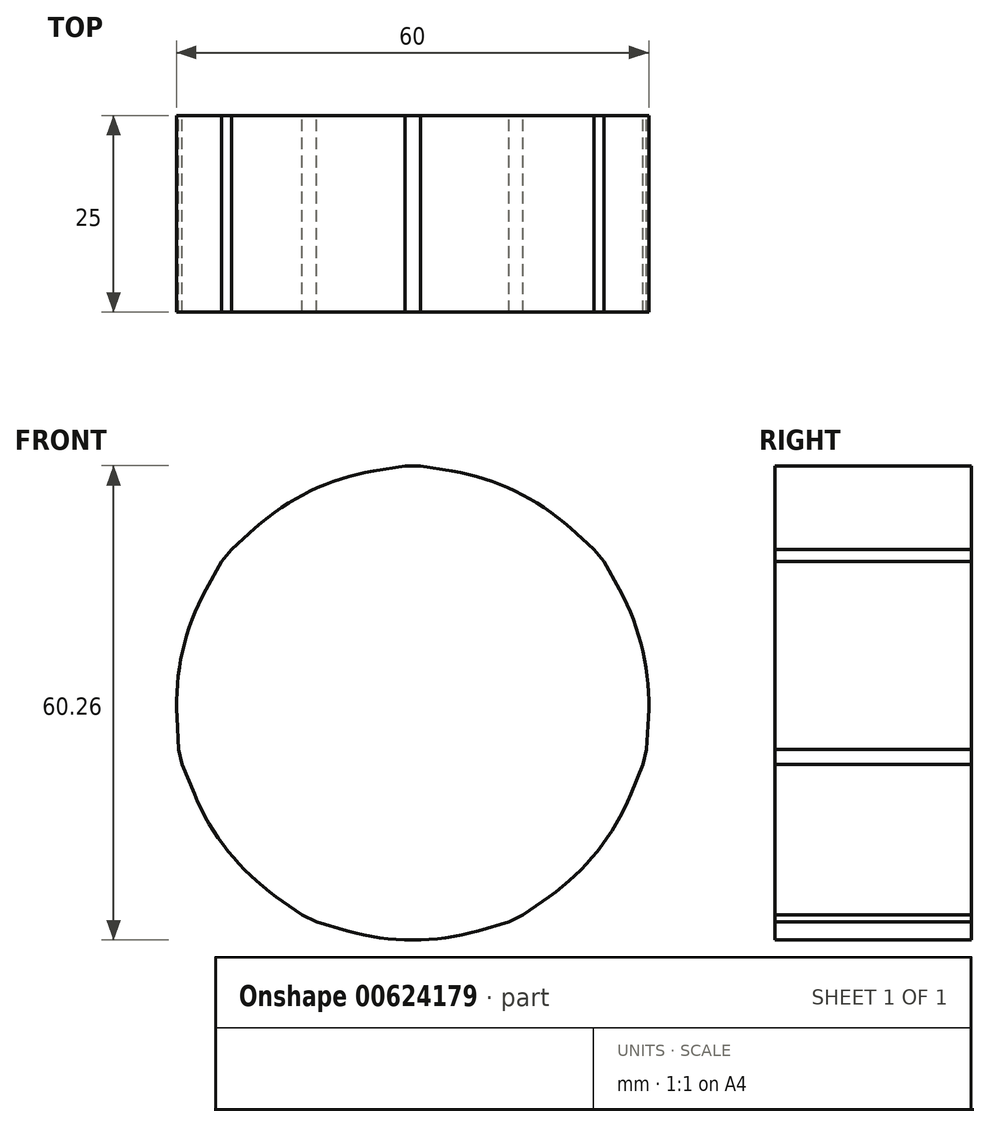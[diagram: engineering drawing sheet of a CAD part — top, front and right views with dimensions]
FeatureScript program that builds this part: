
annotation { "Feature Type Name" : "Feature", "Feature Type Description" : "" }
export const myFeature = defineFeature(function(context is Context, id is Id, definition is map)
    precondition{}
    {
        {
            assignVariable(context, id + "F0", {"name" : "pinon", "anyValue" : 14});
        }
        {
            assignVariable(context, id + "F1", {"name" : "a", "anyValue" : 2});
        }
        {
            assignVariable(context, id + "F2", {"name" : "b", "anyValue" : getVariable(context, 'pinon') / getVariable(context, 'a')});
        }
        {
            var Q0;
            Q0=qCreatedBy(makeId("Front.planeOp"),FACE);
            var sketch = newSketch(context, id + "F3", { "sketchPlane" : qUnion([Q0])});
            skCircle(sketch, "E0", {"center": v(0, 0) * mm, "radius": 30 * mm});
            skLineSegment(sketch, "E1", {"start": v(0, 30.26) * mm, "end": v(1, 30.26) * mm});
            skLineSegment(sketch, "E2", {"start": v(1, 30.26) * mm, "end": v(5, 29.58) * mm});
            skLineSegment(sketch, "E3", {"start": v(0, 55.33) * mm, "end": v(0, 84) * mm, "construction": true});
            skLineSegment(sketch, "E4.MirrorCS", {"start": v(0, 30.26) * mm, "end": v(-1, 30.26) * mm});
            skLineSegment(sketch, "E5.MirrorCS", {"start": v(-1, 30.26) * mm, "end": v(-5, 29.58) * mm});
            skSolve(sketch);
        }
        {
            var Q0;
            Q0=qCreatedBy(makeId("Right.planeOp"),FACE);
            var sketch = newSketch(context, id + "F4", { "sketchPlane" : qUnion([Q0])});
            skLineSegment(sketch, "E6", {"start": v(16.05, 0) * mm, "end": v(51.04, 0) * mm});
            skSolve(sketch);
        }
        {
            var Q0;
            {var subQ0=sQuery(id+"F3.wireOp",EDGE,"E0");var subQ1=makeQuery(id+"F3.imprint","INTERSECT",VERTEX,{"derivedFrom":[subQ0,sQuery(id+"F3.wireOp",EDGE,"E2")]});Q0=makeQuery(id+"F3.imprint","IMPRINT",FACE,{"disambiguationData":[TD([[makeQuery(id+"F3.imprint","IMPRINT",EDGE,{"disambiguationData":[TD([[subQ1,-1.0]])],"derivedFrom":subQ0}),1.0]])]});}
            extrude(context, id + "F5", {"entities" : qUnion([Q0]), "depth" : 25 * mm, "offsetDistance" : 25 * mm});
        }
        {
            var Q0;
            Q0=makeQuery(id+"F3.imprint","IMPRINT",FACE,{"disambiguationData":[TD([[makeQuery(id+"F3.imprint","IMPRINT",EDGE,{"derivedFrom":sQuery(id+"F3.wireOp",EDGE,"E1")}),-1.0]])]});
            extrude(context, id + "F6", {"entities" : qUnion([Q0]), "depth" : 25 * mm, "offsetDistance" : 25 * mm});
        }
        {
            var Q0;
            Q0=makeQuery(id+"F6.opExtrude","SWEPT_BODY",BODY,{"disambiguationData":[OSD([sQuery(id+"F3.wireOp",EDGE,"E0"),sQuery(id+"F3.wireOp",EDGE,"E1"),sQuery(id+"F3.wireOp",EDGE,"E2"),sQuery(id+"F3.wireOp",EDGE,"E4.MirrorCS"),sQuery(id+"F3.wireOp",EDGE,"E5.MirrorCS")])]});
            var Q1;
            Q1=makeQuery(id+"F5.opExtrude","SWEPT_BODY",BODY,{"disambiguationData":[OSD([sQuery(id+"F3.wireOp",EDGE,"E0")])]});
            var Q2;
            Q2=sQuery(id+"F4.wireOp",EDGE,"E6");
            circularPattern(context, id + "F7", {"operationType" : NewBodyOperationType.ADD, "entities" : qUnion([Q0, Q1]), "axis" : qUnion([Q2]), "angle" : 360 * degree, "instanceCount" : getVariable(context, 'b'), "equalSpace" : true});
        }
    });
